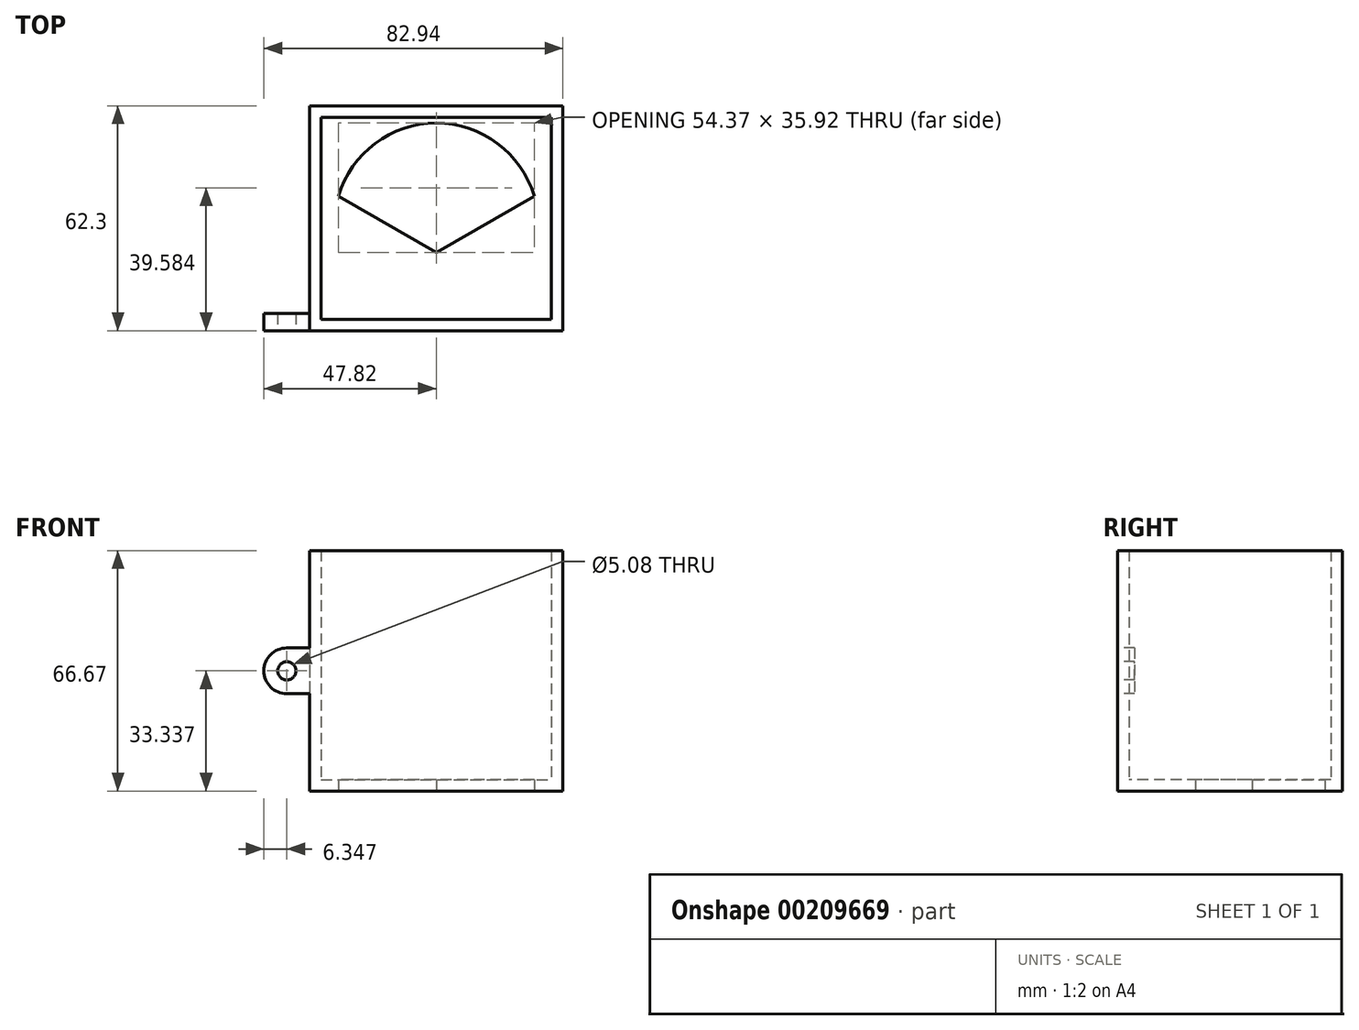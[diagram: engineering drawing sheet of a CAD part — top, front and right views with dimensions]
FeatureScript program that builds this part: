
annotation { "Feature Type Name" : "Feature", "Feature Type Description" : "" }
export const myFeature = defineFeature(function(context is Context, id is Id, definition is map)
    precondition{}
    {
        {
            var Q0;
            Q0=qCreatedBy(makeId("Top.planeOp"),FACE);
            var sketch = newSketch(context, id + "F0", { "sketchPlane" : qUnion([Q0])});
            skLineSegment(sketch, "E0.bottom", {"start": v(31.95, 27.98) * mm, "end": v(-31.95, 27.98) * mm});
            skLineSegment(sketch, "E0.top", {"start": v(31.95, -27.98) * mm, "end": v(-31.95, -27.98) * mm});
            skLineSegment(sketch, "E0.left", {"start": v(31.95, 27.98) * mm, "end": v(31.95, -27.98) * mm});
            skLineSegment(sketch, "E0.right", {"start": v(-31.95, 27.98) * mm, "end": v(-31.95, -27.98) * mm});
            skPoint(sketch, "E0.middle", {"position": v(0, 0) * mm});
            skLineSegment(sketch, "E1.bottom", {"start": v(35.12, 31.15) * mm, "end": v(-35.12, 31.15) * mm});
            skLineSegment(sketch, "E1.top", {"start": v(35.12, -31.15) * mm, "end": v(-35.12, -31.15) * mm});
            skLineSegment(sketch, "E1.left", {"start": v(35.12, 31.15) * mm, "end": v(35.12, -31.15) * mm});
            skLineSegment(sketch, "E1.right", {"start": v(-35.12, 31.15) * mm, "end": v(-35.12, -31.15) * mm});
            skSolve(sketch);
        }
        {
            var Q0;
            Q0 = qSketchRegion(id + "F0", true);
            extrude(context, id + "F1", {"entities" : qUnion([Q0]), "depth" : 66.67 * mm});
        }
        {
            var Q0;
            Q0=qCreatedBy(makeId("Top.planeOp"),FACE);
            var sketch = newSketch(context, id + "F2", { "sketchPlane" : qUnion([Q0])});
            skLineSegment(sketch, "E2.bottom", {"start": v(-31.95, 27.98) * mm, "end": v(31.95, 27.98) * mm});
            skLineSegment(sketch, "E2.top", {"start": v(-31.95, -27.98) * mm, "end": v(31.95, -27.98) * mm});
            skLineSegment(sketch, "E2.left", {"start": v(-31.95, 27.98) * mm, "end": v(-31.95, -27.98) * mm});
            skLineSegment(sketch, "E2.right", {"start": v(31.95, 27.98) * mm, "end": v(31.95, -27.98) * mm});
            skPoint(sketch, "E2.middle", {"position": v(0, 0) * mm});
            skArc(sketch, "E3", {"start": v(27.19, 6.17) * mm, "mid": v(0, 26.4) * mm, "end": v(-27.19, 6.17) * mm});
            skLineSegment(sketch, "E4", {"start": v(27.19, 6.17) * mm, "end": v(0, -9.52) * mm});
            skLineSegment(sketch, "E5", {"start": v(0, -9.52) * mm, "end": v(-27.19, 6.17) * mm});
            skSolve(sketch);
        }
        {
            var Q0;
            Q0 = qSketchRegion(id + "F2", true);
            extrude(context, id + "F3", {"entities" : qUnion([Q0]), "operationType" : NewBodyOperationType.ADD, "depth" : 3.17 * mm});
        }
        {
            var Q0;
            Q0=makeQuery(id+"F1.opExtrude","SWEPT_FACE",FACE,{"disambiguationData":[OSD([sQuery(id+"F0.wireOp",EDGE,"E1.top")])]});
            var sketch = newSketch(context, id + "F4", { "sketchPlane" : qUnion([Q0])});
            skLineSegment(sketch, "E6", {"start": v(-35.12, 39.69) * mm, "end": v(-41.47, 39.69) * mm});
            skLineSegment(sketch, "E7", {"start": v(-41.47, 39.69) * mm, "end": v(-41.47, 26.99) * mm, "construction": true});
            skLineSegment(sketch, "E8", {"start": v(-41.47, 26.99) * mm, "end": v(-35.12, 26.99) * mm});
            skLineSegment(sketch, "E9", {"start": v(-35.12, 26.99) * mm, "end": v(-35.12, 39.69) * mm});
            skArc(sketch, "E10", {"start": v(-41.47, 39.69) * mm, "mid": v(-47.82, 33.34) * mm, "end": v(-41.47, 26.99) * mm});
            skCircle(sketch, "E11", {"center": v(-41.47, 33.34) * mm, "radius": 2.54 * mm});
            skSolve(sketch);
        }
        {
            var Q0;
            Q0 = qSketchRegion(id + "F4", true);
            extrude(context, id + "F5", {"entities" : qUnion([Q0]), "operationType" : NewBodyOperationType.ADD, "oppositeDirection" : true, "depth" : 4.76 * mm});
        }
    });
